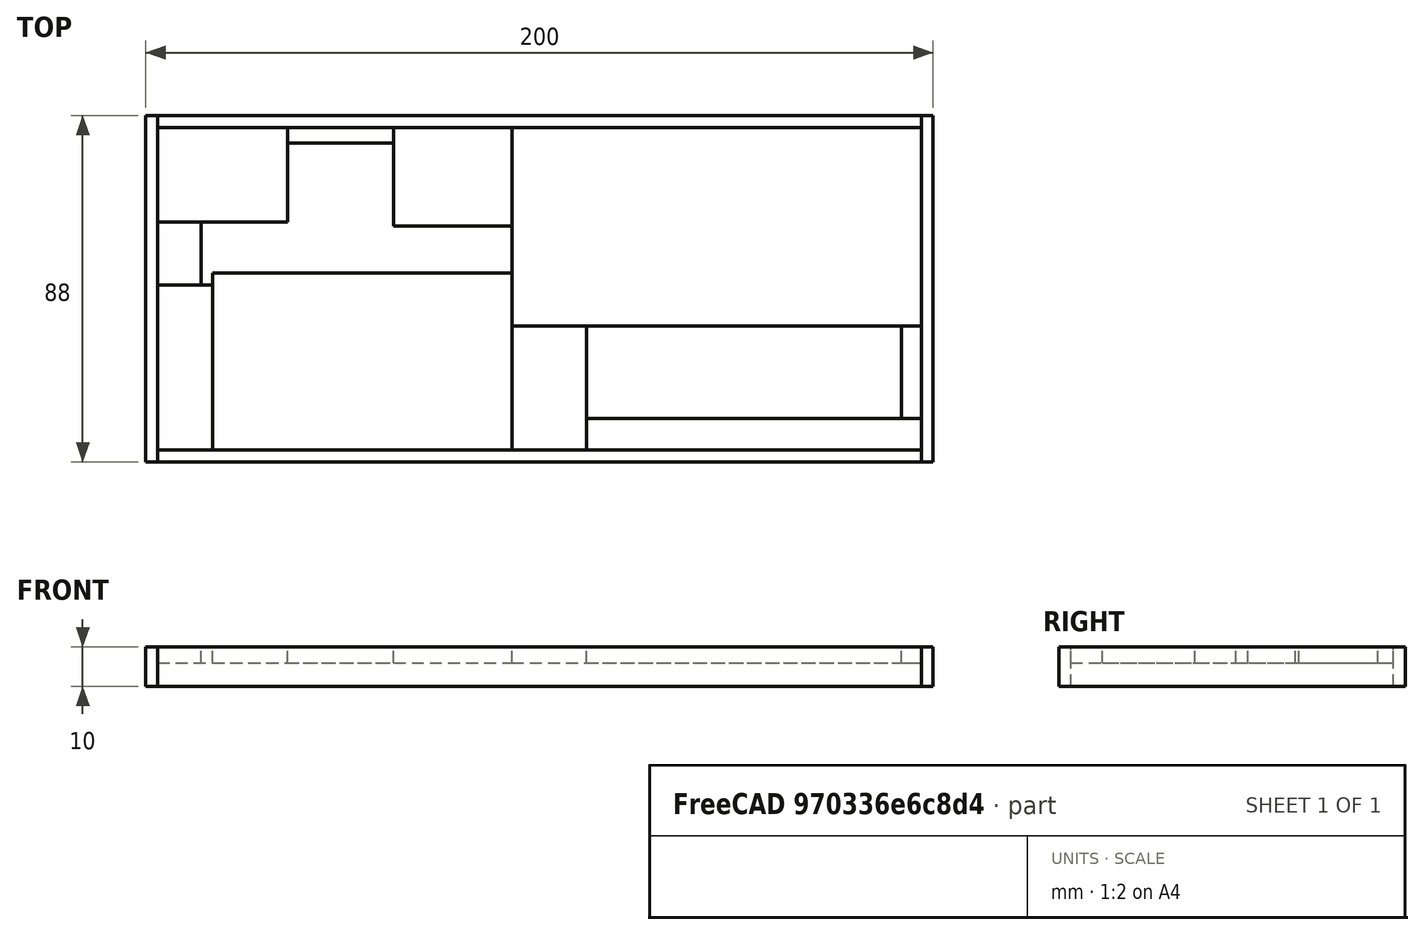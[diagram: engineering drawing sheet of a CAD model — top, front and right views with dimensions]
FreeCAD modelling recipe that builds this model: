
FCSTD DOCUMENT  (FreeCAD 0.15R4671 (Git))
Label: lcd breadboard case - lid
License: All rights reserved
LicenseURL: http://en.wikipedia.org/wiki/All_rights_reserved
objects: Part::Box×14
note: 14 computed .brp shape members not serialized (recipe doc carries the construction recipe); baked Part::Feature solids carry a one-line shape summary decoded from their .brp

FEATURE [Part::Box] Box001  label="cover 001"
  Height = 4
  Length = 85
  Placement = pos=(109,-3,10) rot=(0,0,1;0rad)
  Width = 8
FEATURE [Part::Box] Box002  label="cover 002"
  Height = 4
  Length = 5
  Placement = pos=(189,5,10) rot=(0,0,1;0rad)
  Width = 23.5
FEATURE [Part::Box] Box003  label="cover 003"
  Height = 4
  Length = 104
  Placement = pos=(90,28.5,10) rot=(0,0,1;0rad)
  Width = 50.5
FEATURE [Part::Box] Box004  label="cover 004"
  Height = 4
  Length = 19
  Placement = pos=(90,-3,10) rot=(0,0,1;0rad)
  Width = 31.5
FEATURE [Part::Box] Box005  label="cover 005"
  Height = 4
  Length = 76
  Placement = pos=(14,-3,10) rot=(0,0,1;0rad)
  Width = 45
FEATURE [Part::Box] Box006  label="cover 006"
  Height = 4
  Length = 30
  Placement = pos=(60,54,10) rot=(0,0,1;0rad)
  Width = 25
FEATURE [Part::Box] Box007  label="cover 007"
  Height = 4
  Length = 14
  Placement = pos=(0,-3,10) rot=(0,0,1;0rad)
  Width = 42
FEATURE [Part::Box] Box008  label="cover 008"
  Height = 4
  Length = 33
  Placement = pos=(0,55,10) rot=(0,0,1;0rad)
  Width = 24
FEATURE [Part::Box] Box009  label="cover 009"
  Height = 4
  Length = 11
  Placement = pos=(0,39,10) rot=(0,0,1;0rad)
  Width = 16
FEATURE [Part::Box] Box  label="side 001"
  Height = 10
  Length = 194
  Placement = pos=(0,79,4) rot=(0,0,1;0rad)
  Width = 3
FEATURE [Part::Box] Box011  label="side 003"
  Height = 10
  Length = 3
  Placement = pos=(194,-6,4) rot=(0,0,1;0rad)
  Width = 88
FEATURE [Part::Box] Box012  label="side 004"
  Height = 10
  Length = 3
  Placement = pos=(-3,-6,4) rot=(0,0,1;0rad)
  Width = 88
FEATURE [Part::Box] Box013  label="cover 010"
  Height = 4
  Length = 27
  Placement = pos=(33,75,10) rot=(0,0,1;0rad)
  Width = 4
FEATURE [Part::Box] Box010  label="side 002"
  Height = 10
  Length = 194
  Placement = pos=(0,-6,4) rot=(0,0,1;0rad)
  Width = 3
